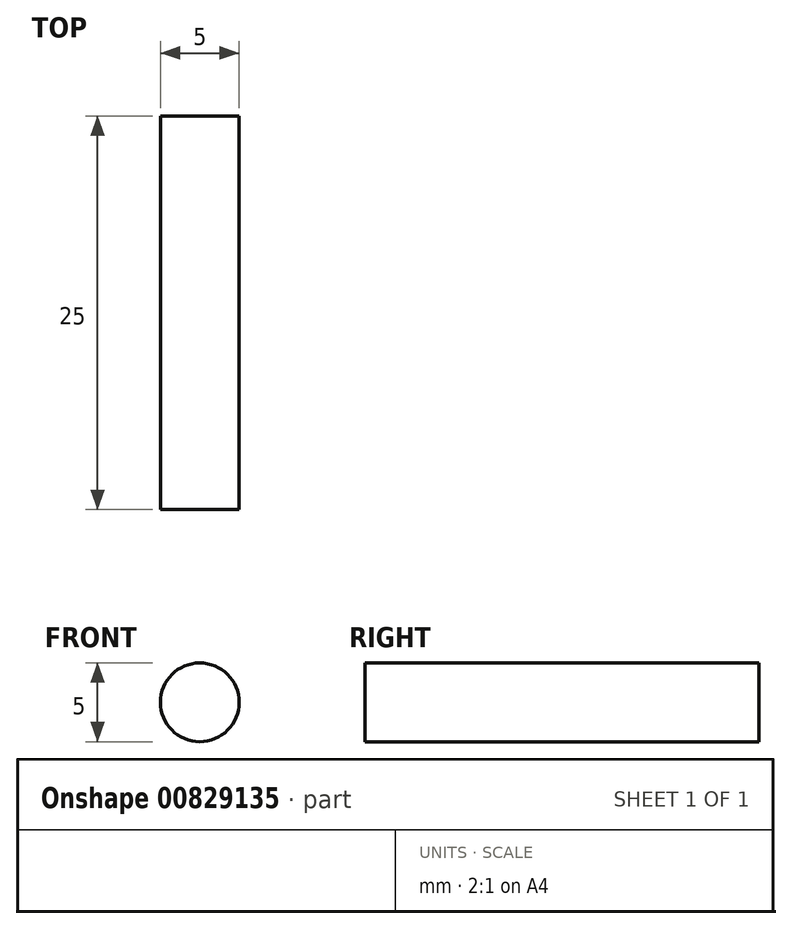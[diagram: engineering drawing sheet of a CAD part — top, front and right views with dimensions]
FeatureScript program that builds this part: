
annotation { "Feature Type Name" : "Feature", "Feature Type Description" : "" }
export const myFeature = defineFeature(function(context is Context, id is Id, definition is map)
    precondition{}
    {
        {
            var Q0;
            Q0=qCreatedBy(makeId("Front.planeOp"),FACE);
            var sketch = newSketch(context, id + "F0", { "sketchPlane" : qUnion([Q0])});
            skCircle(sketch, "E0", {"center": v(0, 0) * mm, "radius": 2.5 * mm});
            skSolve(sketch);
        }
        {
            var Q0;
            Q0 = qSketchRegion(id + "F0", true);
            extrude(context, id + "F1", {"entities" : qUnion([Q0]), "endBound" : BoundingType.SYMMETRIC, "depth" : 25 * mm, "offsetDistance" : 25 * mm});
        }
    });
